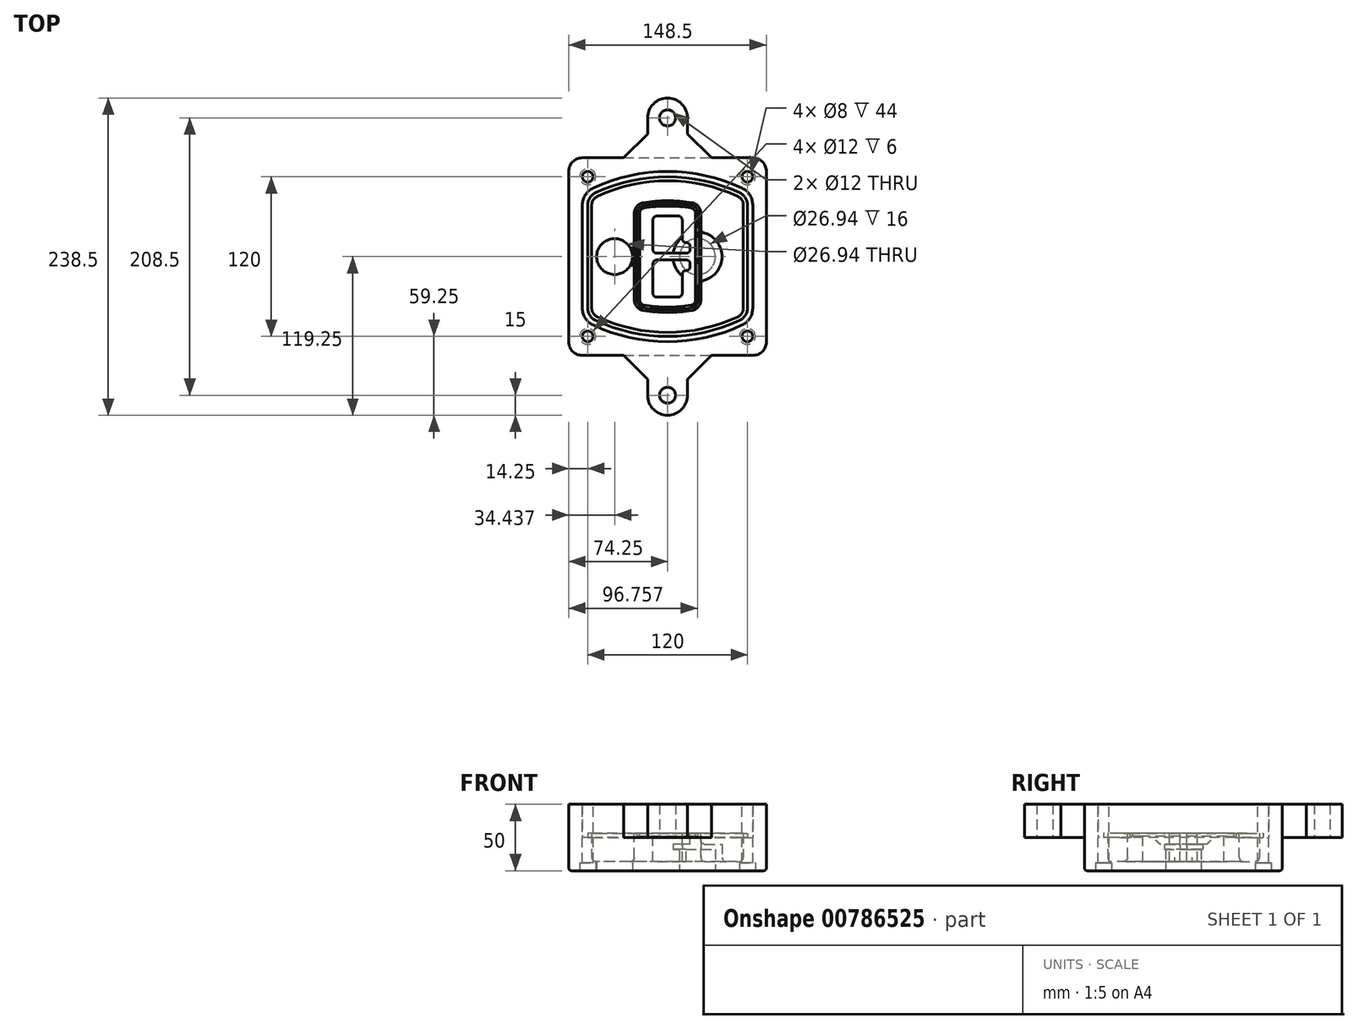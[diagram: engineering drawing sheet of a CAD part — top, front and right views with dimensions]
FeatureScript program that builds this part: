
annotation { "Feature Type Name" : "Feature", "Feature Type Description" : "" }
export const myFeature = defineFeature(function(context is Context, id is Id, definition is map)
    precondition{}
    {
        {
            var Q0;
            Q0=qCreatedBy(makeId("Top.planeOp"),FACE);
            var sketch = newSketch(context, id + "F0", { "sketchPlane" : qUnion([Q0])});
            skPoint(sketch, "E0.rect.middle", {"position": v(0, 0) * mm});
            skLineSegment(sketch, "E1.bottom", {"start": v(-64.25, -74.25) * mm, "end": v(64.25, -74.25) * mm});
            skLineSegment(sketch, "E1.top", {"start": v(-64.25, 74.25) * mm, "end": v(64.25, 74.25) * mm});
            skLineSegment(sketch, "E1.left", {"start": v(-74.25, -64.25) * mm, "end": v(-74.25, 64.25) * mm});
            skLineSegment(sketch, "E1.right", {"start": v(74.25, -64.25) * mm, "end": v(74.25, 64.25) * mm});
            skLineSegment(sketch, "E2", {"start": v(-74.25, 74.25) * mm, "end": v(74.25, -74.25) * mm, "construction": true});
            skLineSegment(sketch, "E3", {"start": v(74.25, 74.25) * mm, "end": v(-74.25, -74.25) * mm, "construction": true});
            skCircle(sketch, "E4", {"center": v(-60, 60) * mm, "radius": 4 * mm});
            skCircle(sketch, "E5", {"center": v(60, 60) * mm, "radius": 4 * mm});
            skCircle(sketch, "E6", {"center": v(60, -60) * mm, "radius": 4 * mm});
            skCircle(sketch, "E7", {"center": v(-60, -60) * mm, "radius": 4 * mm});
            skLineSegment(sketch, "E8", {"start": v(-60, 60) * mm, "end": v(60, 60) * mm, "construction": true});
            skLineSegment(sketch, "E9", {"start": v(60, 60) * mm, "end": v(60, -60) * mm, "construction": true});
            skLineSegment(sketch, "E10", {"start": v(60, -60) * mm, "end": v(-60, -60) * mm, "construction": true});
            skLineSegment(sketch, "E11", {"start": v(-60, -60) * mm, "end": v(-60, 60) * mm, "construction": true});
            skLineSegment(sketch, "E12", {"start": v(-60, 38.83) * mm, "end": v(-60, -38.83) * mm});
            skLineSegment(sketch, "E13", {"start": v(60, 38.83) * mm, "end": v(60, -38.83) * mm});
            skArc(sketch, "E14", {"start": v(54.26, 47.88) * mm, "mid": v(0, 60) * mm, "end": v(-54.26, 47.88) * mm});
            skArc(sketch, "E15", {"start": v(-54.26, -47.88) * mm, "mid": v(0, -60) * mm, "end": v(54.26, -47.88) * mm});
            skLineSegment(sketch, "E16", {"start": v(-60, 0) * mm, "end": v(60, 0) * mm, "construction": true});
            skPoint(sketch, "E17.visualSharp", {"position": v(-60, -45) * mm});
            skArc(sketch, "E17.filletArc", {"start": v(-60, -38.83) * mm, "mid": v(-58.44, -44.2) * mm, "end": v(-54.26, -47.88) * mm});
            skPoint(sketch, "E18.visualSharp", {"position": v(-60, 45) * mm});
            skArc(sketch, "E18.filletArc", {"start": v(-54.26, 47.88) * mm, "mid": v(-58.44, 44.2) * mm, "end": v(-60, 38.83) * mm});
            skPoint(sketch, "E19.visualSharp", {"position": v(60, 45) * mm});
            skArc(sketch, "E19.filletArc", {"start": v(60, 38.83) * mm, "mid": v(58.44, 44.2) * mm, "end": v(54.26, 47.88) * mm});
            skPoint(sketch, "E20.visualSharp", {"position": v(60, -45) * mm});
            skArc(sketch, "E20.filletArc", {"start": v(54.26, -47.88) * mm, "mid": v(58.44, -44.2) * mm, "end": v(60, -38.83) * mm});
            skPoint(sketch, "E21.visualSharp", {"position": v(-74.25, 74.25) * mm});
            skArc(sketch, "E21.filletArc", {"start": v(-64.25, 74.25) * mm, "mid": v(-71.32, 71.32) * mm, "end": v(-74.25, 64.25) * mm});
            skPoint(sketch, "E22.visualSharp", {"position": v(74.25, 74.25) * mm});
            skArc(sketch, "E22.filletArc", {"start": v(74.25, 64.25) * mm, "mid": v(71.32, 71.32) * mm, "end": v(64.25, 74.25) * mm});
            skPoint(sketch, "E23.visualSharp", {"position": v(74.25, -74.25) * mm});
            skArc(sketch, "E23.filletArc", {"start": v(64.25, -74.25) * mm, "mid": v(71.32, -71.32) * mm, "end": v(74.25, -64.25) * mm});
            skPoint(sketch, "E24.visualSharp", {"position": v(-74.25, -74.25) * mm});
            skArc(sketch, "E24.filletArc", {"start": v(-74.25, -64.25) * mm, "mid": v(-71.32, -71.32) * mm, "end": v(-64.25, -74.25) * mm});
            skArc(sketch, "E25.0", {"start": v(57, 38.83) * mm, "mid": v(55.9, 42.58) * mm, "end": v(52.98, 45.17) * mm});
            skLineSegment(sketch, "E25.1", {"start": v(57, 38.83) * mm, "end": v(57, -38.83) * mm});
            skArc(sketch, "E25.2", {"start": v(52.98, -45.17) * mm, "mid": v(55.9, -42.58) * mm, "end": v(57, -38.83) * mm});
            skArc(sketch, "E25.3", {"start": v(-52.98, -45.17) * mm, "mid": v(0, -57) * mm, "end": v(52.98, -45.17) * mm});
            skArc(sketch, "E25.4", {"start": v(-57, -38.83) * mm, "mid": v(-55.9, -42.58) * mm, "end": v(-52.98, -45.17) * mm});
            skArc(sketch, "E25.5", {"start": v(52.98, 45.17) * mm, "mid": v(0, 57) * mm, "end": v(-52.98, 45.17) * mm});
            skLineSegment(sketch, "E25.6", {"start": v(-57, 38.83) * mm, "end": v(-57, -38.83) * mm});
            skArc(sketch, "E25.7", {"start": v(-52.98, 45.17) * mm, "mid": v(-55.9, 42.58) * mm, "end": v(-57, 38.83) * mm});
            skArc(sketch, "E26.0", {"start": v(-55.96, 51.5) * mm, "mid": v(-61.82, 46.33) * mm, "end": v(-64, 38.83) * mm});
            skArc(sketch, "E26.1", {"start": v(55.96, 51.5) * mm, "mid": v(0, 64) * mm, "end": v(-55.96, 51.5) * mm});
            skArc(sketch, "E26.2", {"start": v(64, 38.83) * mm, "mid": v(61.82, 46.33) * mm, "end": v(55.96, 51.5) * mm});
            skLineSegment(sketch, "E26.3", {"start": v(64, 38.83) * mm, "end": v(64, -38.83) * mm});
            skArc(sketch, "E26.4", {"start": v(55.96, -51.5) * mm, "mid": v(61.82, -46.33) * mm, "end": v(64, -38.83) * mm});
            skLineSegment(sketch, "E26.5", {"start": v(-64, 38.83) * mm, "end": v(-64, -38.83) * mm});
            skArc(sketch, "E26.6", {"start": v(-55.96, -51.5) * mm, "mid": v(0, -64) * mm, "end": v(55.96, -51.5) * mm});
            skArc(sketch, "E26.7", {"start": v(-64, -38.83) * mm, "mid": v(-61.82, -46.33) * mm, "end": v(-55.96, -51.5) * mm});
            skLineSegment(sketch, "E27", {"start": v(0, 0) * mm, "end": v(0, 104.25) * mm, "construction": true});
            skPoint(sketch, "E28.visualSharp", {"position": v(-1.46, 136.98) * mm});
            skCircle(sketch, "E29", {"center": v(0, 104.25) * mm, "radius": 6 * mm});
            skLineSegment(sketch, "E30", {"start": v(0, 104.25) * mm, "end": v(-26.7, 104.25) * mm, "construction": true});
            skLineSegment(sketch, "E31", {"start": v(0, 104.25) * mm, "end": v(31.07, 104.25) * mm, "construction": true});
            skArc(sketch, "E32", {"start": v(-15, 104.25) * mm, "mid": v(0, 119.25) * mm, "end": v(15, 104.25) * mm});
            skLineSegment(sketch, "E33", {"start": v(-15, 104.25) * mm, "end": v(-15, 92.25) * mm});
            skLineSegment(sketch, "E34", {"start": v(15, 104.25) * mm, "end": v(15, 92.25) * mm});
            skLineSegment(sketch, "E35", {"start": v(-15, 92.25) * mm, "end": v(-33, 74.25) * mm});
            skLineSegment(sketch, "E36", {"start": v(-33, 74.25) * mm, "end": v(33, 74.25) * mm});
            skLineSegment(sketch, "E37", {"start": v(33, 74.25) * mm, "end": v(15, 92.25) * mm});
            skLineSegment(sketch, "E38.MirrorCS", {"start": v(-15, -92.25) * mm, "end": v(-33, -74.25) * mm});
            skArc(sketch, "E39.MirrorCS", {"start": v(-15, -104.25) * mm, "mid": v(0, -119.25) * mm, "end": v(15, -104.25) * mm});
            skLineSegment(sketch, "E40.MirrorCS", {"start": v(-15, -104.25) * mm, "end": v(-15, -92.25) * mm});
            skLineSegment(sketch, "E41.MirrorCS", {"start": v(-33, -74.25) * mm, "end": v(33, -74.25) * mm});
            skLineSegment(sketch, "E42.MirrorCS", {"start": v(0, -104.25) * mm, "end": v(-26.7, -104.25) * mm, "construction": true});
            skLineSegment(sketch, "E43.MirrorCS", {"start": v(0, -104.25) * mm, "end": v(31.07, -104.25) * mm, "construction": true});
            skLineSegment(sketch, "E44.MirrorCS", {"start": v(33, -74.25) * mm, "end": v(15, -92.25) * mm});
            skCircle(sketch, "E45.MirrorC", {"center": v(0, -104.25) * mm, "radius": 6 * mm});
            skLineSegment(sketch, "E46.MirrorCS", {"start": v(15, -104.25) * mm, "end": v(15, -92.25) * mm});
            skSolve(sketch);
        }
        {
            var Q0;
            Q0=makeQuery(id+"F0.imprint","IMPRINT",FACE,{"disambiguationData":[TD([[makeQuery(id+"F0.imprint","IMPRINT",EDGE,{"derivedFrom":sQuery(id+"F0.wireOp",EDGE,"E1.bottom")}),1.0]])]});
            var Q1;
            Q1=makeQuery(id+"F0.imprint","IMPRINT",FACE,{"disambiguationData":[TD([[makeQuery(id+"F0.imprint","IMPRINT",EDGE,{"derivedFrom":sQuery(id+"F0.wireOp",EDGE,"E12")}),1.0]])]});
            var Q2;
            Q2=makeQuery(id+"F0.imprint","IMPRINT",FACE,{"disambiguationData":[TD([[makeQuery(id+"F0.imprint","IMPRINT",EDGE,{"derivedFrom":sQuery(id+"F0.wireOp",EDGE,"E25.0")}),1.0]])]});
            var Q3;
            Q3=makeQuery(id+"F0.imprint","IMPRINT",FACE,{"disambiguationData":[TD([[makeQuery(id+"F0.imprint","IMPRINT",EDGE,{"derivedFrom":sQuery(id+"F0.wireOp",EDGE,"E12")}),-1.0]])]});
            extrude(context, id + "F1", {"entities" : qUnion([Q0, Q1, Q2, Q3]), "oppositeDirection" : true, "depth" : 25 * mm});
        }
        {
            var Q0;
            Q0=makeQuery(id+"F0.imprint","IMPRINT",FACE,{"disambiguationData":[TD([[makeQuery(id+"F0.imprint","IMPRINT",EDGE,{"derivedFrom":sQuery(id+"F0.wireOp",EDGE,"E12")}),1.0]])]});
            extrude(context, id + "F2", {"entities" : qUnion([Q0]), "operationType" : NewBodyOperationType.ADD, "depth" : 3 * mm});
        }
        {
            var Q0;
            Q0=makeQuery(id+"F0.imprint","IMPRINT",FACE,{"disambiguationData":[TD([[makeQuery(id+"F0.imprint","IMPRINT",EDGE,{"derivedFrom":sQuery(id+"F0.wireOp",EDGE,"E25.0")}),1.0]])]});
            extrude(context, id + "F3", {"entities" : qUnion([Q0]), "operationType" : NewBodyOperationType.REMOVE, "oppositeDirection" : true, "depth" : 18 * mm});
        }
        {
            var Q0;
            Q0=makeQuery(id+"F2.opExtrude","CAP_FACE",FACE,{"disambiguationData":[OSD([sQuery(id+"F0.wireOp",EDGE,"E12"),sQuery(id+"F0.wireOp",EDGE,"E13"),sQuery(id+"F0.wireOp",EDGE,"E14"),sQuery(id+"F0.wireOp",EDGE,"E15"),sQuery(id+"F0.wireOp",EDGE,"E17.filletArc"),sQuery(id+"F0.wireOp",EDGE,"E18.filletArc"),sQuery(id+"F0.wireOp",EDGE,"E19.filletArc"),sQuery(id+"F0.wireOp",EDGE,"E20.filletArc"),sQuery(id+"F0.wireOp",EDGE,"E25.0"),sQuery(id+"F0.wireOp",EDGE,"E25.1"),sQuery(id+"F0.wireOp",EDGE,"E25.2"),sQuery(id+"F0.wireOp",EDGE,"E25.3"),sQuery(id+"F0.wireOp",EDGE,"E25.4"),sQuery(id+"F0.wireOp",EDGE,"E25.5"),sQuery(id+"F0.wireOp",EDGE,"E25.6"),sQuery(id+"F0.wireOp",EDGE,"E25.7")])],"isStart":false});
            var sketch = newSketch(context, id + "F4", { "sketchPlane" : qUnion([Q0])});
            skArc(sketch, "E47.0", {"start": v(-18.34, -40.45) * mm, "mid": v(0, -42) * mm, "end": v(18.34, -40.45) * mm});
            skArc(sketch, "E48.0", {"start": v(18.34, 40.45) * mm, "mid": v(0, 42) * mm, "end": v(-18.34, 40.45) * mm});
            skLineSegment(sketch, "E49", {"start": v(-25, 32.57) * mm, "end": v(-25, -32.57) * mm});
            skLineSegment(sketch, "E50", {"start": v(25, 32.57) * mm, "end": v(25, -32.57) * mm});
            skLineSegment(sketch, "E51", {"start": v(-25, 39.1) * mm, "end": v(25, 39.1) * mm, "construction": true});
            skLineSegment(sketch, "E52", {"start": v(-25, -39.1) * mm, "end": v(25, -39.1) * mm, "construction": true});
            skPoint(sketch, "E53.visualSharp", {"position": v(-25, 39.1) * mm});
            skArc(sketch, "E53.filletArc", {"start": v(-18.34, 40.45) * mm, "mid": v(-23.11, 37.73) * mm, "end": v(-25, 32.57) * mm});
            skPoint(sketch, "E54.visualSharp", {"position": v(25, 39.1) * mm});
            skArc(sketch, "E54.filletArc", {"start": v(25, 32.57) * mm, "mid": v(23.11, 37.73) * mm, "end": v(18.34, 40.45) * mm});
            skPoint(sketch, "E55.visualSharp", {"position": v(25, -39.1) * mm});
            skArc(sketch, "E55.filletArc", {"start": v(18.34, -40.45) * mm, "mid": v(23.11, -37.73) * mm, "end": v(25, -32.57) * mm});
            skPoint(sketch, "E56.visualSharp", {"position": v(-25, -39.1) * mm});
            skArc(sketch, "E56.filletArc", {"start": v(-25, -32.57) * mm, "mid": v(-23.11, -37.73) * mm, "end": v(-18.34, -40.45) * mm});
            skArc(sketch, "E57.0", {"start": v(52.98, 45.17) * mm, "mid": v(0, 57) * mm, "end": v(-52.98, 45.17) * mm});
            skArc(sketch, "E57.1", {"start": v(-52.98, 45.17) * mm, "mid": v(-55.9, 42.58) * mm, "end": v(-57, 38.83) * mm});
            skLineSegment(sketch, "E57.2", {"start": v(-57, 38.83) * mm, "end": v(-57, -38.83) * mm});
            skArc(sketch, "E57.3", {"start": v(-57, -38.83) * mm, "mid": v(-55.9, -42.58) * mm, "end": v(-52.98, -45.17) * mm});
            skArc(sketch, "E57.4", {"start": v(-52.98, -45.17) * mm, "mid": v(0, -57) * mm, "end": v(52.98, -45.17) * mm});
            skArc(sketch, "E57.5", {"start": v(52.98, -45.17) * mm, "mid": v(55.9, -42.58) * mm, "end": v(57, -38.83) * mm});
            skLineSegment(sketch, "E57.6", {"start": v(57, 38.83) * mm, "end": v(57, -38.83) * mm});
            skArc(sketch, "E57.7", {"start": v(57, 38.83) * mm, "mid": v(55.9, 42.58) * mm, "end": v(52.98, 45.17) * mm});
            skLineSegment(sketch, "E58.0", {"start": v(23, 32.57) * mm, "end": v(23, -32.57) * mm});
            skArc(sketch, "E58.1", {"start": v(18, -38.48) * mm, "mid": v(21.58, -36.44) * mm, "end": v(23, -32.57) * mm});
            skArc(sketch, "E58.2", {"start": v(-18, -38.48) * mm, "mid": v(0, -40) * mm, "end": v(18, -38.48) * mm});
            skArc(sketch, "E58.3", {"start": v(-23, -32.57) * mm, "mid": v(-21.58, -36.44) * mm, "end": v(-18, -38.48) * mm});
            skLineSegment(sketch, "E58.4", {"start": v(-23, 32.57) * mm, "end": v(-23, -32.57) * mm});
            skArc(sketch, "E58.5", {"start": v(23, 32.57) * mm, "mid": v(21.58, 36.44) * mm, "end": v(18, 38.48) * mm});
            skArc(sketch, "E58.6", {"start": v(-18, 38.48) * mm, "mid": v(-21.58, 36.44) * mm, "end": v(-23, 32.57) * mm});
            skArc(sketch, "E58.7", {"start": v(18, 38.48) * mm, "mid": v(0, 40) * mm, "end": v(-18, 38.48) * mm});
            skArc(sketch, "E59.0", {"start": v(21, 32.57) * mm, "mid": v(20.06, 35.15) * mm, "end": v(17.67, 36.5) * mm});
            skLineSegment(sketch, "E59.1", {"start": v(21, 32.57) * mm, "end": v(21, -32.57) * mm});
            skArc(sketch, "E59.2", {"start": v(17.67, -36.5) * mm, "mid": v(20.06, -35.15) * mm, "end": v(21, -32.57) * mm});
            skArc(sketch, "E59.3", {"start": v(-17.67, -36.5) * mm, "mid": v(0, -38) * mm, "end": v(17.67, -36.5) * mm});
            skArc(sketch, "E59.4", {"start": v(-21, -32.57) * mm, "mid": v(-20.06, -35.15) * mm, "end": v(-17.67, -36.5) * mm});
            skArc(sketch, "E59.5", {"start": v(17.67, 36.5) * mm, "mid": v(0, 38) * mm, "end": v(-17.67, 36.5) * mm});
            skLineSegment(sketch, "E59.6", {"start": v(-21, 32.57) * mm, "end": v(-21, -32.57) * mm});
            skArc(sketch, "E59.7", {"start": v(-17.67, 36.5) * mm, "mid": v(-20.06, 35.15) * mm, "end": v(-21, 32.57) * mm});
            skLineSegment(sketch, "E60", {"start": v(-25, 0) * mm, "end": v(25, 0) * mm, "construction": true});
            skLineSegment(sketch, "E61", {"start": v(-11, 5.5) * mm, "end": v(-11, 27.5) * mm});
            skLineSegment(sketch, "E62", {"start": v(-8, 30.5) * mm, "end": v(8, 30.5) * mm});
            skLineSegment(sketch, "E63", {"start": v(11, 27.5) * mm, "end": v(11, 13.5) * mm});
            skLineSegment(sketch, "E64", {"start": v(14, 10.5) * mm, "end": v(14, 10.5) * mm});
            skLineSegment(sketch, "E65", {"start": v(17, 7.5) * mm, "end": v(17, 5.5) * mm});
            skLineSegment(sketch, "E66", {"start": v(14, 2.5) * mm, "end": v(-8, 2.5) * mm});
            skPoint(sketch, "E67.visualSharp", {"position": v(-11, 30.5) * mm});
            skArc(sketch, "E67.filletArc", {"start": v(-8, 30.5) * mm, "mid": v(-10.12, 29.62) * mm, "end": v(-11, 27.5) * mm});
            skPoint(sketch, "E68.visualSharp", {"position": v(11, 30.5) * mm});
            skArc(sketch, "E68.filletArc", {"start": v(11, 27.5) * mm, "mid": v(10.12, 29.62) * mm, "end": v(8, 30.5) * mm});
            skPoint(sketch, "E69.visualSharp", {"position": v(11, 10.5) * mm});
            skArc(sketch, "E69.filletArc", {"start": v(11, 13.5) * mm, "mid": v(11.88, 11.38) * mm, "end": v(14, 10.5) * mm});
            skPoint(sketch, "E70.visualSharp", {"position": v(17, 10.5) * mm});
            skArc(sketch, "E70.filletArc", {"start": v(17, 7.5) * mm, "mid": v(16.12, 9.62) * mm, "end": v(14, 10.5) * mm});
            skPoint(sketch, "E71.visualSharp", {"position": v(17, 2.5) * mm});
            skArc(sketch, "E71.filletArc", {"start": v(14, 2.5) * mm, "mid": v(16.12, 3.38) * mm, "end": v(17, 5.5) * mm});
            skPoint(sketch, "E72.visualSharp", {"position": v(-11, 2.5) * mm});
            skArc(sketch, "E72.filletArc", {"start": v(-11, 5.5) * mm, "mid": v(-10.12, 3.38) * mm, "end": v(-8, 2.5) * mm});
            skLineSegment(sketch, "E73.0.MirrorCS", {"start": v(14, -2.5) * mm, "end": v(-8, -2.5) * mm});
            skArc(sketch, "E74.0.MirrorCS", {"start": v(-11, -5.5) * mm, "mid": v(-10.12, -3.38) * mm, "end": v(-8, -2.5) * mm});
            skLineSegment(sketch, "E75.0.MirrorCS", {"start": v(-11, -5.5) * mm, "end": v(-11, -27.5) * mm});
            skArc(sketch, "E76.0.MirrorCS", {"start": v(-8, -30.5) * mm, "mid": v(-10.12, -29.62) * mm, "end": v(-11, -27.5) * mm});
            skLineSegment(sketch, "E77.0.MirrorCS", {"start": v(-8, -30.5) * mm, "end": v(8, -30.5) * mm});
            skArc(sketch, "E78.0.MirrorCS", {"start": v(11, -27.5) * mm, "mid": v(10.12, -29.62) * mm, "end": v(8, -30.5) * mm});
            skLineSegment(sketch, "E79.0.MirrorCS", {"start": v(11, -27.5) * mm, "end": v(11, -13.5) * mm});
            skArc(sketch, "E80.0.MirrorCS", {"start": v(11, -13.5) * mm, "mid": v(11.88, -11.38) * mm, "end": v(14, -10.5) * mm});
            skArc(sketch, "E81.0.MirrorCS", {"start": v(17, -7.5) * mm, "mid": v(16.12, -9.62) * mm, "end": v(14, -10.5) * mm});
            skLineSegment(sketch, "E82.0.MirrorCS", {"start": v(17, -7.5) * mm, "end": v(17, -5.5) * mm});
            skArc(sketch, "E83.0.MirrorCS", {"start": v(14, -2.5) * mm, "mid": v(16.12, -3.38) * mm, "end": v(17, -5.5) * mm});
            skSolve(sketch);
        }
        {
            var Q0;
            Q0=makeQuery(id+"F4.imprint","IMPRINT",FACE,{"disambiguationData":[TD([[makeQuery(id+"F4.imprint","IMPRINT",EDGE,{"derivedFrom":sQuery(id+"F4.wireOp",EDGE,"E47.0")}),1.0]])]});
            var Q1;
            Q1=makeQuery(id+"F4.imprint","IMPRINT",FACE,{"disambiguationData":[TD([[makeQuery(id+"F4.imprint","IMPRINT",EDGE,{"derivedFrom":sQuery(id+"F4.wireOp",EDGE,"E58.0")}),-1.0]])]});
            var Q2;
            Q2=makeQuery(id+"F4.imprint","IMPRINT",FACE,{"disambiguationData":[TD([[makeQuery(id+"F4.imprint","IMPRINT",EDGE,{"derivedFrom":sQuery(id+"F4.wireOp",EDGE,"E59.0")}),1.0]])]});
            extrude(context, id + "F5", {"entities" : qUnion([Q0, Q1, Q2]), "operationType" : NewBodyOperationType.ADD, "endBound" : BoundingType.UP_TO_NEXT, "oppositeDirection" : true, "depth" : 25 * mm});
        }
        {
            var Q0;
            Q0=makeQuery(id+"F4.imprint","IMPRINT",FACE,{"disambiguationData":[TD([[makeQuery(id+"F4.imprint","IMPRINT",EDGE,{"derivedFrom":sQuery(id+"F4.wireOp",EDGE,"E58.0")}),-1.0]])]});
            extrude(context, id + "F6", {"entities" : qUnion([Q0]), "operationType" : NewBodyOperationType.REMOVE, "oppositeDirection" : true, "depth" : 2 * mm});
        }
        {
            var Q0;
            Q0=makeQuery(id+"F1.opExtrude","CAP_FACE",FACE,{"disambiguationData":[OSD([sQuery(id+"F0.wireOp",EDGE,"E1.bottom"),sQuery(id+"F0.wireOp",EDGE,"E1.top"),sQuery(id+"F0.wireOp",EDGE,"E1.left"),sQuery(id+"F0.wireOp",EDGE,"E1.right"),sQuery(id+"F0.wireOp",EDGE,"E4"),sQuery(id+"F0.wireOp",EDGE,"E5"),sQuery(id+"F0.wireOp",EDGE,"E6"),sQuery(id+"F0.wireOp",EDGE,"E7"),sQuery(id+"F0.wireOp",EDGE,"E21.filletArc"),sQuery(id+"F0.wireOp",EDGE,"E22.filletArc"),sQuery(id+"F0.wireOp",EDGE,"E23.filletArc"),sQuery(id+"F0.wireOp",EDGE,"E24.filletArc")])],"isStart":false});
            var sketch = newSketch(context, id + "F7", { "sketchPlane" : qUnion([Q0])});
            skCircle(sketch, "E84", {"center": v(22.5, 0) * mm, "radius": 13.47 * mm});
            skCircle(sketch, "E85", {"center": v(-39.81, 0) * mm, "radius": 13.47 * mm});
            skLineSegment(sketch, "E86", {"start": v(74.25, 0) * mm, "end": v(-74.25, 0) * mm});
            skCircle(sketch, "E87", {"center": v(22.5, 0) * mm, "radius": 18.47 * mm});
            skCircle(sketch, "E88", {"center": v(60, -60) * mm, "radius": 6 * mm});
            skCircle(sketch, "E89", {"center": v(-60, -60) * mm, "radius": 6 * mm});
            skCircle(sketch, "E90", {"center": v(-60, 60) * mm, "radius": 6 * mm});
            skCircle(sketch, "E91", {"center": v(60, 60) * mm, "radius": 6 * mm});
            skSolve(sketch);
        }
        {
            var Q0;
            {var subQ1=sQuery(id+"F7.wireOp",EDGE,"E86");var subQ4=sQuery(id+"F7.wireOp",EDGE,"E84");var subQ6=makeQuery(id+"F7.imprint","INTERSECT",VERTEX,{"disambiguationData":[OD(0.0)],"derivedFrom":[subQ4,subQ1]});Q0=makeQuery(id+"F7.imprint","IMPRINT",FACE,{"disambiguationData":[TD([[makeQuery(id+"F7.imprint","IMPRINT",EDGE,{"disambiguationData":[TD([[subQ6,-1.0]])],"derivedFrom":subQ4}),-1.0]])]});}
            var Q1;
            {var subQ0=sQuery(id+"F7.wireOp",EDGE,"E86");var subQ1=sQuery(id+"F7.wireOp",EDGE,"E84");var subQ3=makeQuery(id+"F7.imprint","INTERSECT",VERTEX,{"disambiguationData":[OD(0.0)],"derivedFrom":[subQ1,subQ0]});Q1=makeQuery(id+"F7.imprint","IMPRINT",FACE,{"disambiguationData":[TD([[makeQuery(id+"F7.imprint","IMPRINT",EDGE,{"disambiguationData":[TD([[subQ3,-1.0]])],"derivedFrom":subQ1}),1.0]])]});}
            var Q2;
            {var subQ0=sQuery(id+"F7.wireOp",EDGE,"E86");var subQ1=sQuery(id+"F7.wireOp",EDGE,"E84");var subQ3=makeQuery(id+"F7.imprint","INTERSECT",VERTEX,{"disambiguationData":[OD(0.0)],"derivedFrom":[subQ1,subQ0]});Q2=makeQuery(id+"F7.imprint","IMPRINT",FACE,{"disambiguationData":[TD([[makeQuery(id+"F7.imprint","IMPRINT",EDGE,{"disambiguationData":[TD([[subQ3,1.0]])],"derivedFrom":subQ1}),1.0]])]});}
            var Q3;
            {var subQ1=sQuery(id+"F7.wireOp",EDGE,"E86");var subQ4=sQuery(id+"F7.wireOp",EDGE,"E84");var subQ6=makeQuery(id+"F7.imprint","INTERSECT",VERTEX,{"disambiguationData":[OD(0.0)],"derivedFrom":[subQ4,subQ1]});Q3=makeQuery(id+"F7.imprint","IMPRINT",FACE,{"disambiguationData":[TD([[makeQuery(id+"F7.imprint","IMPRINT",EDGE,{"disambiguationData":[TD([[subQ6,1.0]])],"derivedFrom":subQ4}),-1.0]])]});}
            extrude(context, id + "F8", {"entities" : qUnion([Q0, Q1, Q2, Q3]), "operationType" : NewBodyOperationType.ADD, "oppositeDirection" : true, "depth" : 20 * mm});
        }
        {
            var Q0;
            {var subQ0=sQuery(id+"F7.wireOp",EDGE,"E86");var subQ1=sQuery(id+"F7.wireOp",EDGE,"E84");var subQ3=makeQuery(id+"F7.imprint","INTERSECT",VERTEX,{"disambiguationData":[OD(0.0)],"derivedFrom":[subQ1,subQ0]});Q0=makeQuery(id+"F7.imprint","IMPRINT",FACE,{"disambiguationData":[TD([[makeQuery(id+"F7.imprint","IMPRINT",EDGE,{"disambiguationData":[TD([[subQ3,-1.0]])],"derivedFrom":subQ1}),1.0]])]});}
            var Q1;
            {var subQ0=sQuery(id+"F7.wireOp",EDGE,"E86");var subQ1=sQuery(id+"F7.wireOp",EDGE,"E84");var subQ3=makeQuery(id+"F7.imprint","INTERSECT",VERTEX,{"disambiguationData":[OD(0.0)],"derivedFrom":[subQ1,subQ0]});Q1=makeQuery(id+"F7.imprint","IMPRINT",FACE,{"disambiguationData":[TD([[makeQuery(id+"F7.imprint","IMPRINT",EDGE,{"disambiguationData":[TD([[subQ3,1.0]])],"derivedFrom":subQ1}),1.0]])]});}
            extrude(context, id + "F9", {"entities" : qUnion([Q0, Q1]), "operationType" : NewBodyOperationType.REMOVE, "oppositeDirection" : true, "depth" : 16 * mm});
        }
        {
            var Q0;
            {var subQ0=sQuery(id+"F7.wireOp",EDGE,"E86");var subQ1=sQuery(id+"F7.wireOp",EDGE,"E85");var subQ3=makeQuery(id+"F7.imprint","INTERSECT",VERTEX,{"disambiguationData":[OD(0.0)],"derivedFrom":[subQ1,subQ0]});Q0=makeQuery(id+"F7.imprint","IMPRINT",FACE,{"disambiguationData":[TD([[makeQuery(id+"F7.imprint","IMPRINT",EDGE,{"disambiguationData":[TD([[subQ3,-1.0]])],"derivedFrom":subQ1}),1.0]])]});}
            var Q1;
            {var subQ0=sQuery(id+"F7.wireOp",EDGE,"E86");var subQ1=sQuery(id+"F7.wireOp",EDGE,"E85");var subQ3=makeQuery(id+"F7.imprint","INTERSECT",VERTEX,{"disambiguationData":[OD(0.0)],"derivedFrom":[subQ1,subQ0]});Q1=makeQuery(id+"F7.imprint","IMPRINT",FACE,{"disambiguationData":[TD([[makeQuery(id+"F7.imprint","IMPRINT",EDGE,{"disambiguationData":[TD([[subQ3,1.0]])],"derivedFrom":subQ1}),1.0]])]});}
            extrude(context, id + "F10", {"entities" : qUnion([Q0, Q1]), "operationType" : NewBodyOperationType.REMOVE, "oppositeDirection" : true, "depth" : 25 * mm});
        }
        {
            var Q0;
            Q0=makeQuery(id+"F7.imprint","IMPRINT",FACE,{"disambiguationData":[TD([[makeQuery(id+"F7.imprint","IMPRINT",EDGE,{"derivedFrom":sQuery(id+"F7.wireOp",EDGE,"E88")}),1.0]])]});
            var Q1;
            Q1=makeQuery(id+"F7.imprint","IMPRINT",FACE,{"disambiguationData":[TD([[makeQuery(id+"F7.imprint","IMPRINT",EDGE,{"derivedFrom":makeQuery(id+"F1.opExtrude","CAP_EDGE",EDGE,{"disambiguationData":[OSD([sQuery(id+"F0.wireOp",EDGE,"E5")])],"isStart":false})}),-1.0]])]});
            var Q2;
            Q2=makeQuery(id+"F7.imprint","IMPRINT",FACE,{"disambiguationData":[TD([[makeQuery(id+"F7.imprint","IMPRINT",EDGE,{"derivedFrom":sQuery(id+"F7.wireOp",EDGE,"E89")}),1.0]])]});
            var Q3;
            Q3=makeQuery(id+"F7.imprint","IMPRINT",FACE,{"disambiguationData":[TD([[makeQuery(id+"F7.imprint","IMPRINT",EDGE,{"derivedFrom":makeQuery(id+"F1.opExtrude","CAP_EDGE",EDGE,{"disambiguationData":[OSD([sQuery(id+"F0.wireOp",EDGE,"E4")])],"isStart":false})}),-1.0]])]});
            var Q4;
            Q4=makeQuery(id+"F7.imprint","IMPRINT",FACE,{"disambiguationData":[TD([[makeQuery(id+"F7.imprint","IMPRINT",EDGE,{"derivedFrom":sQuery(id+"F7.wireOp",EDGE,"E90")}),1.0]])]});
            var Q5;
            Q5=makeQuery(id+"F7.imprint","IMPRINT",FACE,{"disambiguationData":[TD([[makeQuery(id+"F7.imprint","IMPRINT",EDGE,{"derivedFrom":makeQuery(id+"F1.opExtrude","CAP_EDGE",EDGE,{"disambiguationData":[OSD([sQuery(id+"F0.wireOp",EDGE,"E7")])],"isStart":false})}),-1.0]])]});
            var Q6;
            Q6=makeQuery(id+"F7.imprint","IMPRINT",FACE,{"disambiguationData":[TD([[makeQuery(id+"F7.imprint","IMPRINT",EDGE,{"derivedFrom":sQuery(id+"F7.wireOp",EDGE,"E91")}),1.0]])]});
            var Q7;
            Q7=makeQuery(id+"F7.imprint","IMPRINT",FACE,{"disambiguationData":[TD([[makeQuery(id+"F7.imprint","IMPRINT",EDGE,{"derivedFrom":makeQuery(id+"F1.opExtrude","CAP_EDGE",EDGE,{"disambiguationData":[OSD([sQuery(id+"F0.wireOp",EDGE,"E6")])],"isStart":false})}),-1.0]])]});
            extrude(context, id + "F11", {"entities" : qUnion([Q0, Q1, Q2, Q3, Q4, Q5, Q6, Q7]), "operationType" : NewBodyOperationType.REMOVE, "oppositeDirection" : true, "depth" : 6 * mm});
        }
        {
            var Q0;
            Q0=makeQuery(id+"F9.boolean.opBoolean","COPY",FACE,{"derivedFrom":makeQuery(id+"F9.opExtrude","CAP_FACE",FACE,{"disambiguationData":[OSD([sQuery(id+"F7.wireOp",EDGE,"E84")])],"isStart":false})});
            var sketch = newSketch(context, id + "F12", { "sketchPlane" : qUnion([Q0])});
            skArc(sketch, "E92.0", {"start": v(11, 14.45) * mm, "mid": v(6.45, 9.13) * mm, "end": v(4.2, 2.5) * mm});
            skArc(sketch, "E92.1", {"start": v(4.2, -2.5) * mm, "mid": v(6.45, -9.13) * mm, "end": v(11, -14.45) * mm});
            skLineSegment(sketch, "E93", {"start": v(4.2, -2.5) * mm, "end": v(14, -2.5) * mm});
            skLineSegment(sketch, "E94.0", {"start": v(14, 2.5) * mm, "end": v(4.2, 2.5) * mm});
            skArc(sketch, "E94.1", {"start": v(14, 2.5) * mm, "mid": v(16.12, 3.38) * mm, "end": v(17, 5.5) * mm});
            skLineSegment(sketch, "E94.2", {"start": v(17, 7.5) * mm, "end": v(17, 5.5) * mm});
            skArc(sketch, "E94.3", {"start": v(17, 7.5) * mm, "mid": v(16.12, 9.62) * mm, "end": v(14, 10.5) * mm});
            skArc(sketch, "E94.4", {"start": v(11, 13.5) * mm, "mid": v(11.88, 11.38) * mm, "end": v(14, 10.5) * mm});
            skLineSegment(sketch, "E94.5", {"start": v(11, 14.45) * mm, "end": v(11, 13.5) * mm});
            skLineSegment(sketch, "E94.7", {"start": v(14, -2.5) * mm, "end": v(4.2, -2.5) * mm});
            skArc(sketch, "E94.8", {"start": v(14, -2.5) * mm, "mid": v(16.12, -3.38) * mm, "end": v(17, -5.5) * mm});
            skLineSegment(sketch, "E94.9", {"start": v(17, -7.5) * mm, "end": v(17, -5.5) * mm});
            skArc(sketch, "E94.10", {"start": v(17, -7.5) * mm, "mid": v(16.12, -9.62) * mm, "end": v(14, -10.5) * mm});
            skArc(sketch, "E94.11", {"start": v(11, -13.5) * mm, "mid": v(11.88, -11.38) * mm, "end": v(14, -10.5) * mm});
            skLineSegment(sketch, "E94.12", {"start": v(11, -14.45) * mm, "end": v(11, -13.5) * mm});
            skPoint(sketch, "E95.orphan", {"position": v(11, -27.5) * mm});
            skPoint(sketch, "E96.orphan", {"position": v(-8, -2.5) * mm});
            skPoint(sketch, "E97.orphan", {"position": v(-8, 2.5) * mm});
            skPoint(sketch, "E98.orphan", {"position": v(11, 27.5) * mm});
            skSolve(sketch);
        }
        {
            var Q0;
            {var subQ7=sQuery(id+"F12.wireOp",EDGE,"E92.0");var subQ14=sQuery(id+"F12.wireOp",EDGE,"E92.1");var subQ16=sQuery(id+"F12.wireOp",EDGE,"E94.1");var subQ18=sQuery(id+"F12.wireOp",EDGE,"E94.8");Q0=qUnion([makeQuery(id+"F12.imprint","IMPRINT",FACE,{"disambiguationData":[TD([[makeQuery(id+"F12.imprint","IMPRINT",EDGE,{"derivedFrom":subQ7}),1.0]])]}),makeQuery(id+"F12.imprint","IMPRINT",FACE,{"disambiguationData":[TD([[makeQuery(id+"F12.imprint","IMPRINT",EDGE,{"derivedFrom":subQ14}),1.0]])]}),makeQuery(id+"F12.imprint","IMPRINT",FACE,{"disambiguationData":[TD([[makeQuery(id+"F12.imprint","IMPRINT",EDGE,{"derivedFrom":subQ16}),1.0]])]}),makeQuery(id+"F12.imprint","IMPRINT",FACE,{"disambiguationData":[TD([[makeQuery(id+"F12.imprint","IMPRINT",EDGE,{"derivedFrom":subQ18}),-1.0]])]})]);}
            var Q1;
            Q1=makeQuery(id+"F5.boolean.opBoolean","SPLIT",FACE,{"disambiguationData":[TD([makeQuery(id+"F5.opExtrude","SWEPT_FACE",FACE,{"disambiguationData":[OSD([sQuery(id+"F4.wireOp",EDGE,"E61")])]})])],"derivedFrom":makeQuery(id+"F3.boolean.opBoolean","COPY",FACE,{"derivedFrom":makeQuery(id+"F3.opExtrude","CAP_FACE",FACE,{"disambiguationData":[OSD([sQuery(id+"F0.wireOp",EDGE,"E25.0"),sQuery(id+"F0.wireOp",EDGE,"E25.1"),sQuery(id+"F0.wireOp",EDGE,"E25.2"),sQuery(id+"F0.wireOp",EDGE,"E25.3"),sQuery(id+"F0.wireOp",EDGE,"E25.4"),sQuery(id+"F0.wireOp",EDGE,"E25.5"),sQuery(id+"F0.wireOp",EDGE,"E25.6"),sQuery(id+"F0.wireOp",EDGE,"E25.7")])],"isStart":false})})});
            extrude(context, id + "F13", {"entities" : qUnion([Q0]), "operationType" : NewBodyOperationType.REMOVE, "endBound" : BoundingType.UP_TO_SURFACE, "endBoundEntityFace" : qUnion([Q1]), "depth" : 25 * mm});
        }
        {
            var Q0;
            Q0=makeQuery(id+"F3.boolean.opBoolean","COPY",EDGE,{"derivedFrom":makeQuery(id+"F3.opExtrude","CAP_EDGE",EDGE,{"disambiguationData":[OSD([sQuery(id+"F0.wireOp",EDGE,"E25.6")])],"isStart":false})});
            var Q1;
            Q1=makeQuery(id+"F8.boolean.opBoolean","INTERSECT",EDGE,{"derivedFrom":[makeQuery(id+"F5.opExtrude","SWEPT_FACE",FACE,{"disambiguationData":[OSD([sQuery(id+"F4.wireOp",EDGE,"E50")])]}),makeQuery(id+"F8.opExtrude","CAP_FACE",FACE,{"disambiguationData":[OSD([sQuery(id+"F7.wireOp",EDGE,"E87")])],"isStart":false})]});
            var Q2;
            Q2=makeQuery(id+"F8.boolean.opBoolean","INTERSECT",EDGE,{"disambiguationData":[OD(1.0)],"derivedFrom":[makeQuery(id+"F5.opExtrude","SWEPT_FACE",FACE,{"disambiguationData":[OSD([sQuery(id+"F4.wireOp",EDGE,"E50")])]}),makeQuery(id+"F8.opExtrude","SWEPT_FACE",FACE,{"disambiguationData":[OSD([sQuery(id+"F7.wireOp",EDGE,"E87")])]})]});
            var Q3;
            {var subQ0=sQuery(id+"F4.wireOp",EDGE,"E50");Q3=makeQuery(id+"F8.boolean.opBoolean","SPLIT",EDGE,{"disambiguationData":[TD([makeQuery(id+"F5.opExtrude","SWEPT_FACE",FACE,{"disambiguationData":[OSD([sQuery(id+"F4.wireOp",EDGE,"E55.filletArc")])]})])],"derivedFrom":makeQuery(id+"F5.opExtrude","CAP_EDGE",EDGE,{"disambiguationData":[OSD([subQ0])],"isStart":false})});}
            var Q4;
            {var subQ0=sQuery(id+"F0.wireOp",EDGE,"E25.7");var subQ1=sQuery(id+"F0.wireOp",EDGE,"E25.1");var subQ2=sQuery(id+"F0.wireOp",EDGE,"E25.6");var subQ3=sQuery(id+"F0.wireOp",EDGE,"E25.5");var subQ4=sQuery(id+"F0.wireOp",EDGE,"E25.4");var subQ5=sQuery(id+"F0.wireOp",EDGE,"E25.0");var subQ6=sQuery(id+"F0.wireOp",EDGE,"E25.2");var subQ7=sQuery(id+"F0.wireOp",EDGE,"E25.3");Q4=makeQuery(id+"F8.boolean.opBoolean","INTERSECT",EDGE,{"derivedFrom":[makeQuery(id+"F5.boolean.opBoolean","SPLIT",FACE,{"disambiguationData":[TD([makeQuery(id+"F2.opExtrude","SWEPT_FACE",FACE,{"disambiguationData":[OSD([subQ5])]})])],"derivedFrom":makeQuery(id+"F3.boolean.opBoolean","COPY",FACE,{"derivedFrom":makeQuery(id+"F3.opExtrude","CAP_FACE",FACE,{"disambiguationData":[OSD([subQ5,subQ1,subQ6,subQ7,subQ4,subQ3,subQ2,subQ0])],"isStart":false})})}),makeQuery(id+"F8.opExtrude","SWEPT_FACE",FACE,{"disambiguationData":[OSD([sQuery(id+"F7.wireOp",EDGE,"E87")])]})]});}
            var Q5;
            Q5=makeQuery(id+"F8.boolean.opBoolean","INTERSECT",EDGE,{"disambiguationData":[OD(0.0)],"derivedFrom":[makeQuery(id+"F5.opExtrude","SWEPT_FACE",FACE,{"disambiguationData":[OSD([sQuery(id+"F4.wireOp",EDGE,"E50")])]}),makeQuery(id+"F8.opExtrude","SWEPT_FACE",FACE,{"disambiguationData":[OSD([sQuery(id+"F7.wireOp",EDGE,"E87")])]})]});
            fillet(context, id + "F14", {"entities" : qUnion([Q0, Q1, Q2, Q3, Q4, Q5]), "radius" : 3 * mm, "tangentPropagation" : true, "allowEdgeOverflow" : false});
        }
        {
            var Q0;
            Q0=makeQuery(id+"F1.opExtrude","CAP_EDGE",EDGE,{"disambiguationData":[OSD([sQuery(id+"F0.wireOp",EDGE,"E1.bottom")])],"isStart":false});
            fillet(context, id + "F15", {"entities" : qUnion([Q0]), "radius" : 2 * mm, "tangentPropagation" : true, "allowEdgeOverflow" : false});
        }
        {
            var Q0;
            Q0 = qSketchRegion(id + "F0", true);
            extrude(context, id + "F16", {"entities" : qUnion([Q0]), "operationType" : NewBodyOperationType.ADD, "depth" : 25 * mm, "offsetDistance" : 25 * mm});
        }
    });
